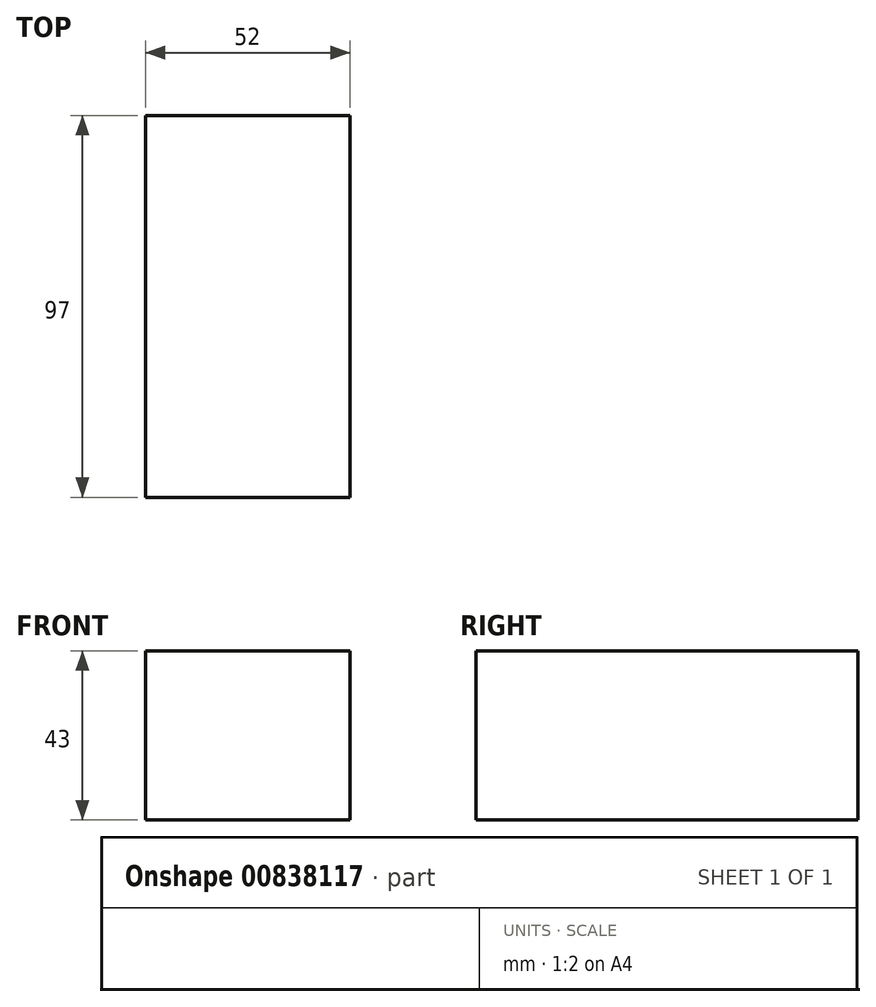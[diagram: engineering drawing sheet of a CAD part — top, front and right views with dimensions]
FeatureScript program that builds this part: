
annotation { "Feature Type Name" : "Feature", "Feature Type Description" : "" }
export const myFeature = defineFeature(function(context is Context, id is Id, definition is map)
    precondition{}
    {
        {
            var Q0;
            Q0=qCreatedBy(makeId("Top.planeOp"),FACE);
            var sketch = newSketch(context, id + "F0", { "sketchPlane" : qUnion([Q0])});
            skLineSegment(sketch, "E0.bottom", {"start": v(26, -48.5) * mm, "end": v(-26, -48.5) * mm});
            skLineSegment(sketch, "E0.top", {"start": v(26, 48.5) * mm, "end": v(-26, 48.5) * mm});
            skLineSegment(sketch, "E0.left", {"start": v(26, -48.5) * mm, "end": v(26, 48.5) * mm});
            skLineSegment(sketch, "E0.right", {"start": v(-26, -48.5) * mm, "end": v(-26, 48.5) * mm});
            skPoint(sketch, "E0.middle", {"position": v(0, 0) * mm});
            skSolve(sketch);
        }
        {
            var Q0;
            Q0=makeQuery(id+"F0.imprint","IMPRINT",FACE,{"disambiguationData":[TD([[makeQuery(id+"F0.imprint","IMPRINT",EDGE,{"derivedFrom":sQuery(id+"F0.wireOp",EDGE,"E0.bottom")}),-1.0]])]});
            extrude(context, id + "F1", {"entities" : qUnion([Q0]), "depth" : 43 * mm, "offsetDistance" : 25 * mm});
        }
    });
